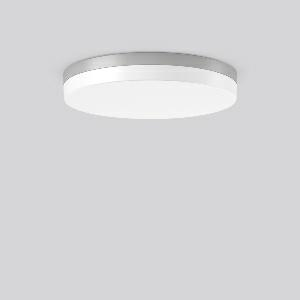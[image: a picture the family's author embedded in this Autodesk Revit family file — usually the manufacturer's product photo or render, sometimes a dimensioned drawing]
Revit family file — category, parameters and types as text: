
# Revit family: flat_slim_round_312678_004_1_19_5c64
name_source: partatom
category: Lighting Fixtures
units: mm (PartAtom-declared; Revit-internal decimal feet)

## family parameters
Cut with Voids When Loaded = No
Host = Face
Light Source = No
Part Type = Normal
Room Calculation Point = No
Round Connector Dimension = Use Diameter
Shared = No

## types (1)
- MultiLumen 1 830 (1 x LED Modul 830, 3500 lm, 3000)
    Apparent Load = 24 VA
    CIE Flux Codes = 38 68 89 85 100
    Color Rendering = 80
    Color Temperature = 3000
    Default Elevation = 1800 mm
    Height = 70 mm
    Lamp = 1 x LED Modul 830
    Lamp Light Flux = 3500 lm
    Lamp count = 1
    Length = 480 mm
    Lifetime = 50000 h
    Luminous efficacy = 146 lm/W
    Manufacturer = RZB
    ModVariant = No
    Model = 312678.004.1.19
    Mounting Place = Ceiling
    Mounting Type = Surface mounted
    Number of Poles = 1
    OnlyDefault = Yes
    Power Factor = 1
    Product Name = FLAT SLIM round
    Product group = Surface mounted ceiling and wall luminaires
    ProductGroupID = 305
    Protection Class = Protection class I
    Protection Degree = Degree of protection
    RLX_Detail_Level = 1
    RLX_Emergency_Light_Flux = 0 lm
    RLX_Emergency_Type = 0
    RLX_Emergency_Type_DB = No
    RlxData = <blob elided: 22465 chars, md5=f1ee4fb1>
    Socket = socket
    Standby Power = 0 W
    System Light Flux = 3500 lm
    System Power = 24 W
    Type Comments = MultiLumen 1 830
    Type Image = 312633.004.jpg
    URL = http://relux.com
    VarID = multilumen_1_830
    Voltage = 0 V
    Weight = 0.00 kg
    Width = 0 mm  [stored 0 ft]

note: [stored X ft] marks values corroborated as IEEE doubles in the binary element streams (Revit-internal decimal feet)

## geometry (parser evidence)
native form markers: Blend x4, Sweep x13
no freeform markers — native parametric forms only
